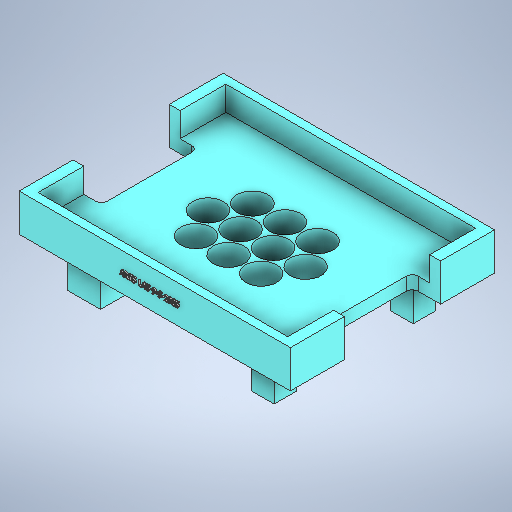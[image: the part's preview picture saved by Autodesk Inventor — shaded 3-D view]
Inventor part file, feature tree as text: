
AUTODESK INVENTOR PART (.ipt)
format: ipt  version: 2025.2 (Build 292293000, 293)  size: 1,937,920 bytes
history: native  units: mm
features: projected_geometry x10, extrude x9, sketch x9
ambient origin geometry x8: Origin, YZ Plane, XZ Plane, XY Plane, X Axis, Y Axis, Z Axis, Center Point
bodies: Solid1 (feature_tree)
feature tree (28):
  extrude  "Extrusion1"  Depth=19.0mm
  sketch  "Sketch4"  dims[d4=19.0mm d6=19.0mm]
  extrude  "Extrusion7"  Depth=19.0mm
  sketch  "Sketch5"  dims[d8=19.0mm d10=19.0mm]
  extrude  "Extrusion8"  Depth=19.0mm
  extrude  "Extrusion6"  Depth=19.0mm
  extrude  "Extrusion9"  Depth=15.0mm TaperAngle=0.0deg
  extrude  "Extrusion11"  Depth=1.0mm
  extrude  "Extrusion12"  Depth=7.23mm
  extrude  "Extrusion14"  Depth=7.23mm
  extrude  "Extrusion15"  TaperAngle=0.0deg  [1 undecoded]
  sketch  "Sketch1"  dims[d0=19.0mm d2=19.0mm]
  projected_geometry  "Projected Loop1"
  sketch  "Sketch6"  dims[d11=19.0mm d13=19.0mm]
  projected_geometry  "Projected Loop4"
  sketch  "Sketch7"  dims[d14=19.0mm]
  projected_geometry  "Projected Loop5"
  projected_geometry  "Projected Loop6"
  sketch  "Sketch10"  dims[d16=20.0mm d17=20.0mm d18=20.0mm d19=20.0mm d20=20.0mm d21=20.0mm d22=20.0mm d23=20.0mm d24=15.0mm d25=0.0mm]
  projected_geometry  "Projected Loop9"
  sketch  "Sketch11"  dims[d53=19.0mm d91=1.0mm]
  projected_geometry  "Projected Loop10"
  projected_geometry  "Projected Loop11"
  sketch  "Sketch13"  dims[d104=153.4mm d123=7.23mm]
  projected_geometry  "Projected Loop13"
  projected_geometry  "Projected Loop14"
  sketch  "Sketch14"  dims[d124=7.23mm d125=7.23mm d126=0.0mm d127=0.0mm d140=7.23mm d144=21.0mm d145=21.0mm d146=21.0mm d147=21.0mm d148=21.0mm d149=21.0mm d150=21.0mm d151=21.0mm d152=21.0mm d153=21.0mm d154=23.0mm d155=23.0mm d156=23.0mm d157=23.0mm d158=23.0mm d159=23.0mm d160=23.0mm d161=23.0mm d162=23.0mm d163=23.0mm d164=115.4mm d165=8.0mm d166=0.0mm d169=5.0mm d170=6.646447mm d171=166.692894mm d172=125.4mm d173=15.0mm d174=8.0mm d175=0.0mm d176=0.0mm d177=0.0mm d178=0.0mm d179=31.75mm d180=7.228mm d181=7.228mm d182=31.75mm d183=31.75mm d184=7.228mm d185=7.228mm d186=31.75mm d209=30.0mm d210=20.0mm d211=20.0mm d212=20.0mm d213=15.0mm d214=15.0mm d215=30.0mm d216=20.0mm d217=14.0mm d218=14.0mm d219=25.0mm d220=0.0mm d221=6.646447mm d222=70.0mm d223=0.0mm d224=30.0mm d225=30.0mm d226=20.0mm d227=20.0mm d231=10.0mm d232=0.0mm d233=76.7mm d234=76.7mm d235=17.489447mm d236=17.489447mm d237=1.0mm d238=0.0mm d228=0.5mm d229=0.872665mm d230=0.5mm]
  projected_geometry  "Projected Loop15"
note: 1 required parameter value undecoded (feature->parameter linkage not recoverable at this tier; creation-order binding heuristic only, values carry confidence <= 0.55)
